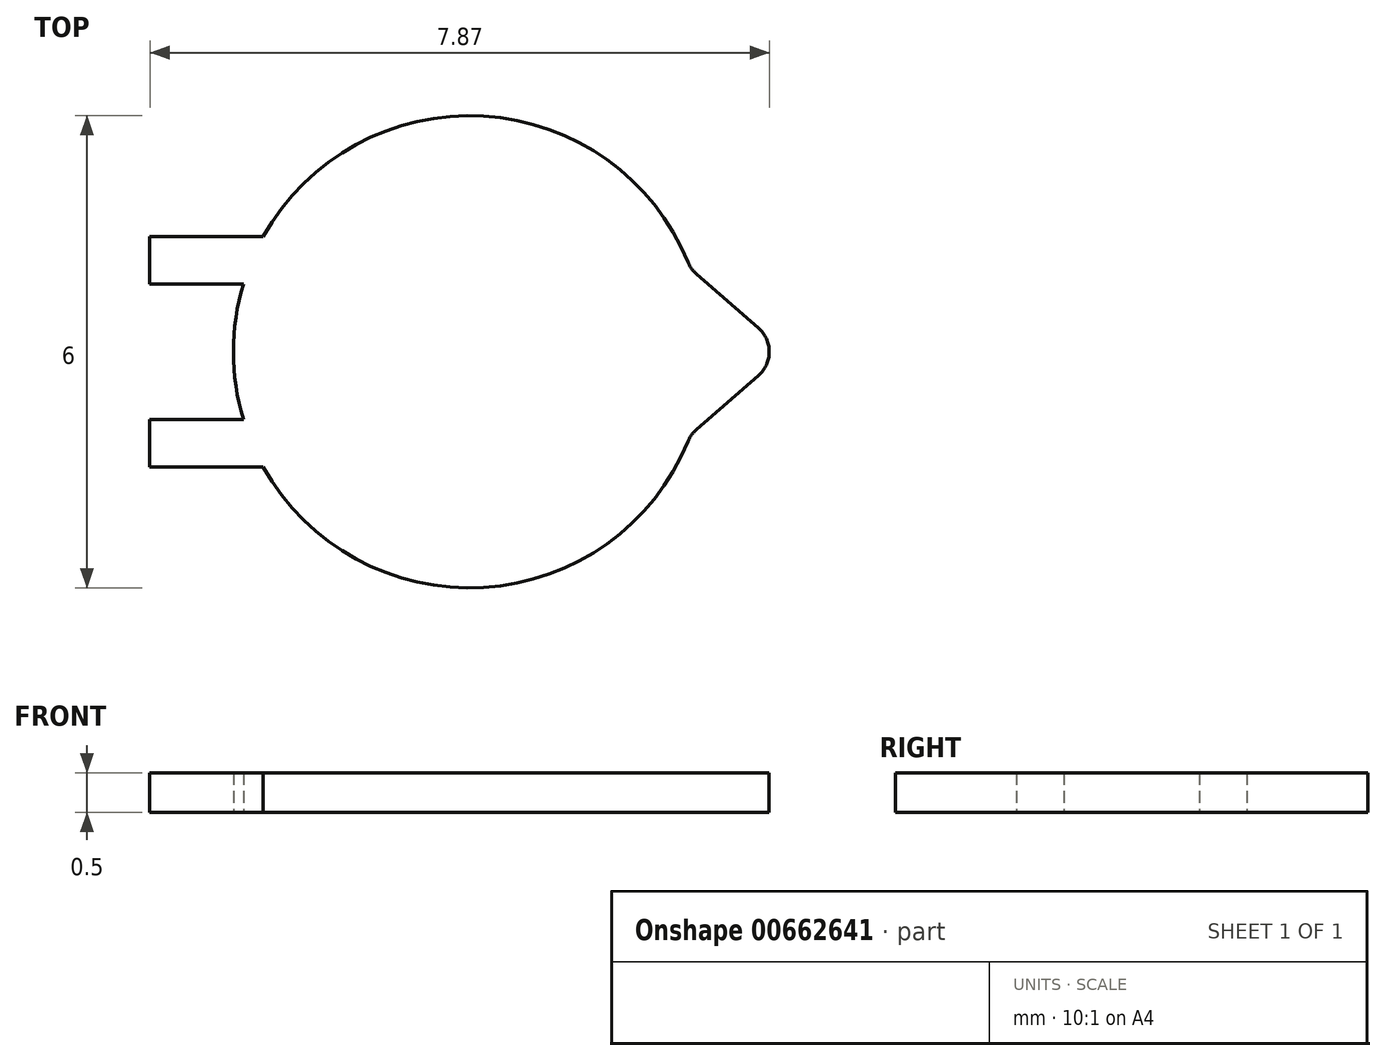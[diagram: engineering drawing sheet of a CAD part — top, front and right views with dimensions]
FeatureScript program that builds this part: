
annotation { "Feature Type Name" : "Feature", "Feature Type Description" : "" }
export const myFeature = defineFeature(function(context is Context, id is Id, definition is map)
    precondition{}
    {
        {
            var Q0;
            Q0=qCreatedBy(makeId("Top.planeOp"),FACE);
            var sketch = newSketch(context, id + "F0", { "sketchPlane" : qUnion([Q0])});
            skArc(sketch, "E0", {"start": v(-2.87, 0.86) * mm, "mid": v(-3, 0) * mm, "end": v(-2.87, -0.86) * mm});
            skLineSegment(sketch, "E1", {"start": v(-4.06, -0.86) * mm, "end": v(-4.06, -1.46) * mm});
            skLineSegment(sketch, "E2", {"start": v(-4.06, -1.46) * mm, "end": v(-2.62, -1.46) * mm});
            skLineSegment(sketch, "E3", {"start": v(-4.06, -0.86) * mm, "end": v(-2.87, -0.86) * mm});
            skLineSegment(sketch, "E4", {"start": v(2.8, -1.05) * mm, "end": v(4.01, 0) * mm});
            skLineSegment(sketch, "E5.MirrorCS", {"start": v(-4.06, 0.86) * mm, "end": v(-4.06, 1.46) * mm});
            skLineSegment(sketch, "E6.MirrorCS", {"start": v(-4.06, 1.46) * mm, "end": v(-2.62, 1.46) * mm});
            skLineSegment(sketch, "E7.MirrorCS", {"start": v(-4.06, 0.86) * mm, "end": v(-2.87, 0.86) * mm});
            skLineSegment(sketch, "E8.MirrorCS", {"start": v(2.8, 1.05) * mm, "end": v(4.01, 0) * mm});
            skArc(sketch, "E9.trimOffspring", {"start": v(2.8, 1.05) * mm, "mid": v(0.23, 3) * mm, "end": v(-2.62, 1.46) * mm});
            skArc(sketch, "E10.trimOffspring", {"start": v(-2.62, -1.46) * mm, "mid": v(0.23, -3) * mm, "end": v(2.8, -1.05) * mm});
            skSolve(sketch);
        }
        {
            var Q0;
            Q0=makeQuery(id+"F0.imprint","IMPRINT",FACE,{"disambiguationData":[TD([[makeQuery(id+"F0.imprint","IMPRINT",EDGE,{"derivedFrom":sQuery(id+"F0.wireOp",EDGE,"E0")}),1.0]])]});
            extrude(context, id + "F1", {"entities" : qUnion([Q0]), "depth" : .5 * mm, "offsetDistance" : 25 * mm});
        }
        {
            var Q0;
            Q0=makeQuery(id+"F1.opExtrude","SWEPT_EDGE",EDGE,{"disambiguationData":[OSD([sQuery(id+"F0.wireOp",EDGE,"E4"),sQuery(id+"F0.wireOp",EDGE,"E8.MirrorCS")])]});
            var Q1;
            Q1=makeQuery(id+"F1.opExtrude","SWEPT_EDGE",EDGE,{"disambiguationData":[OSD([sQuery(id+"F0.wireOp",EDGE,"E8.MirrorCS"),sQuery(id+"F0.wireOp",EDGE,"E9.trimOffspring")])]});
            var Q2;
            Q2=makeQuery(id+"F1.opExtrude","SWEPT_EDGE",EDGE,{"disambiguationData":[OSD([sQuery(id+"F0.wireOp",EDGE,"E4"),sQuery(id+"F0.wireOp",EDGE,"E10.trimOffspring")])]});
            fillet(context, id + "F2", {"entities" : qUnion([Q0, Q1, Q2]), "radius" : .4 * mm, "tangentPropagation" : true, "allowEdgeOverflow" : false});
        }
    });
